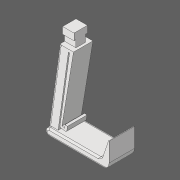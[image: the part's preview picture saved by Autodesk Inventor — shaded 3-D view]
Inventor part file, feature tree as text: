
AUTODESK INVENTOR PART (.ipt)
format: ipt  version: 2020 (Build 240168000, 168)  size: 253,440 bytes
history: native  units: in
note: dims shown in document units (in); Inventor stores cm internally (conversion verified against a paired STEP export)
features: fillet x5, other x3, extrude x3
ambient origin geometry x8: Origin, YZ Plane, XZ Plane, XY Plane, X Axis, Y Axis, Z Axis, Center Point
bodies: Solid1 (feature_tree)
feature tree (11):
  other  "Neck Start Plane"
  other  "Arm Profile"
  extrude  "Main Arm"  Depth=0.0039in
  extrude  "Pincher"  Depth=1.0386in
  extrude  "Neck"  Depth=0.6299in
  fillet  "Spring Hook Fillet"  Radius=0.1181in
  fillet  "Spring Attachment Fillet"  [1 undecoded]
  fillet  "Soft Edges"  Radius=0.1941in
  fillet  "Pincher Fillet 1"  Radius=0.0197in
  fillet  "Pincher Fillet 2"  Radius=0.0394in
  other  "Neck Sketch"
note: 1 required parameter value undecoded (feature->parameter linkage not recoverable at this tier; creation-order binding heuristic only, values carry confidence <= 0.55)
